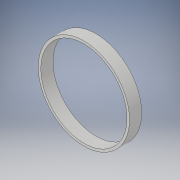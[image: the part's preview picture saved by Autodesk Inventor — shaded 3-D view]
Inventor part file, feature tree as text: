
AUTODESK INVENTOR PART (.ipt)
format: ipt  version: 2019 (Build 230136000, 136)  size: 102,912 bytes
history: native  units: mm
features: extrude x1, sketch x1
ambient origin geometry x8: Origin, YZ Plane, XZ Plane, XY Plane, X Axis, Y Axis, Z Axis, Center Point
bodies: Solid1 (feature_tree)
feature tree (2):
  extrude  "Extrusion1"  Depth=24.0mm
  sketch  "Sketch1"  dims[d0=180.0mm d1=170.0mm d2=24.0mm d3=0.0mm]
